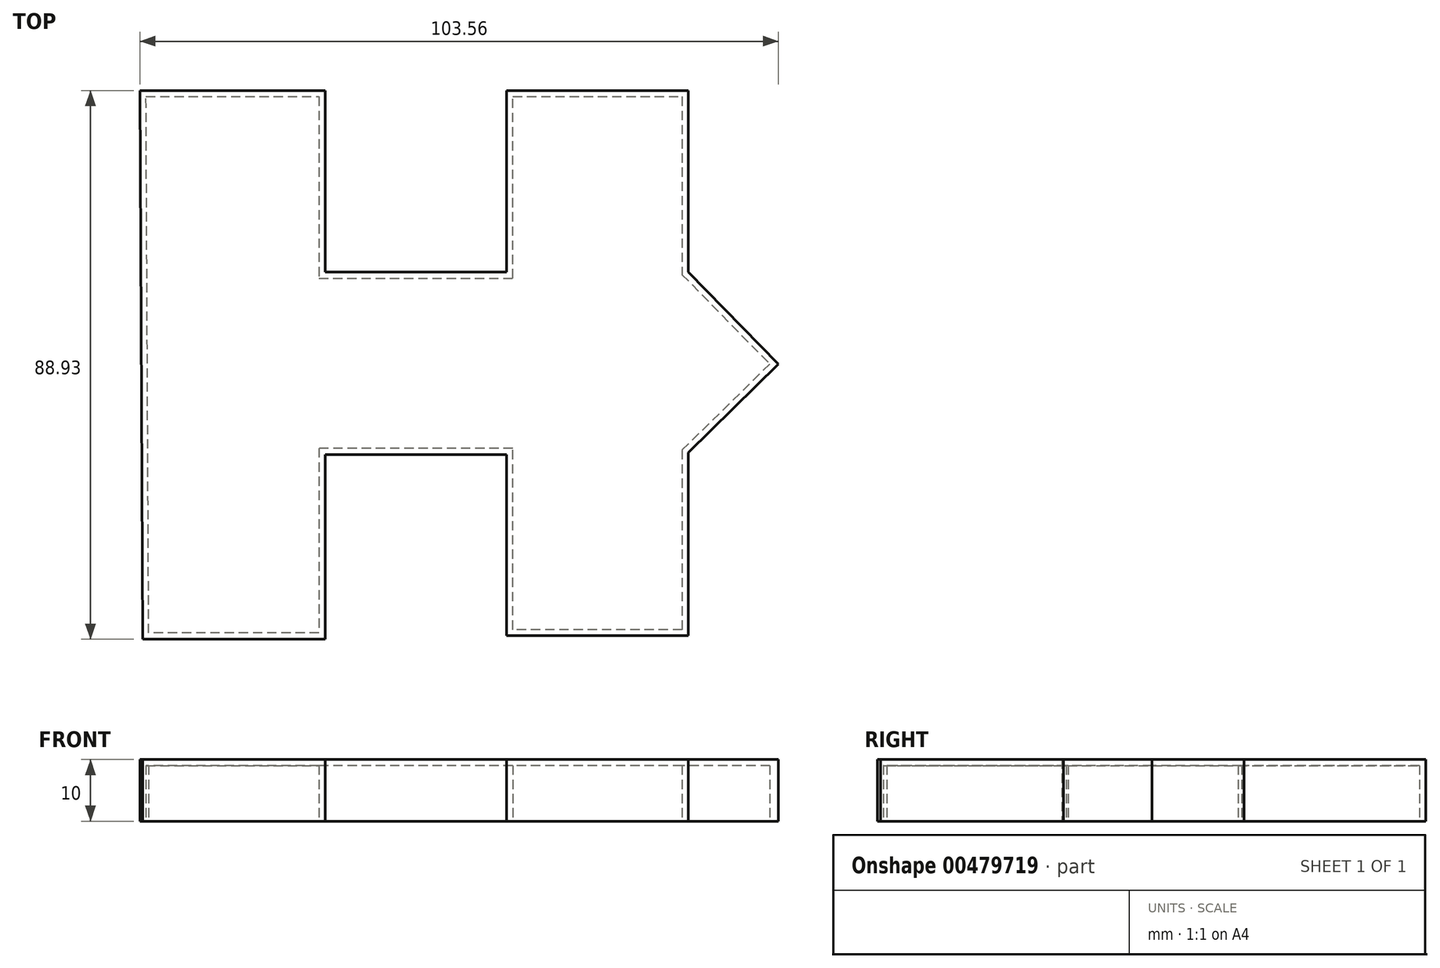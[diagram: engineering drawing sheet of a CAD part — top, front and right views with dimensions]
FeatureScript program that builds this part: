
annotation { "Feature Type Name" : "Feature", "Feature Type Description" : "" }
export const myFeature = defineFeature(function(context is Context, id is Id, definition is map)
    precondition{}
    {
        {
            var Q0;
            Q0=qCreatedBy(makeId("Top.planeOp"),FACE);
            var sketch = newSketch(context, id + "F0", { "sketchPlane" : qUnion([Q0])});
            skLineSegment(sketch, "E0", {"start": v(-44.76, 44.35) * mm, "end": v(-14.71, 44.35) * mm});
            skLineSegment(sketch, "E1", {"start": v(-14.71, 44.35) * mm, "end": v(-14.71, 14.91) * mm});
            skLineSegment(sketch, "E2", {"start": v(-14.71, 14.91) * mm, "end": v(14.73, 14.91) * mm});
            skLineSegment(sketch, "E3", {"start": v(14.73, 14.91) * mm, "end": v(14.73, 44.35) * mm});
            skLineSegment(sketch, "E4", {"start": v(14.73, 44.35) * mm, "end": v(44.17, 44.35) * mm});
            skLineSegment(sketch, "E5", {"start": v(44.17, 44.35) * mm, "end": v(44.17, 14.91) * mm});
            skLineSegment(sketch, "E6", {"start": v(44.17, 14.91) * mm, "end": v(58.8, 0) * mm});
            skLineSegment(sketch, "E7", {"start": v(58.8, 0) * mm, "end": v(44.17, -14.36) * mm});
            skLineSegment(sketch, "E8", {"start": v(44.17, -14.36) * mm, "end": v(44.17, -44.03) * mm});
            skLineSegment(sketch, "E9", {"start": v(44.17, -44.03) * mm, "end": v(14.73, -44.03) * mm});
            skLineSegment(sketch, "E10", {"start": v(14.73, -44.03) * mm, "end": v(14.73, -14.64) * mm});
            skLineSegment(sketch, "E11", {"start": v(14.73, -14.64) * mm, "end": v(-14.71, -14.64) * mm});
            skLineSegment(sketch, "E12", {"start": v(-14.71, -14.64) * mm, "end": v(-14.71, -44.58) * mm});
            skLineSegment(sketch, "E13", {"start": v(-14.71, -44.58) * mm, "end": v(-44.32, -44.58) * mm});
            skLineSegment(sketch, "E14", {"start": v(-44.32, -44.58) * mm, "end": v(-44.76, 44.35) * mm});
            skSolve(sketch);
        }
        {
            var Q0;
            Q0=makeQuery(id+"F0.imprint","IMPRINT",FACE,{"disambiguationData":[TD([[makeQuery(id+"F0.imprint","IMPRINT",EDGE,{"derivedFrom":sQuery(id+"F0.wireOp",EDGE,"E0")}),-1.0]])]});
            extrude(context, id + "F1", {"entities" : qUnion([Q0]), "depth" : 10 * mm});
        }
        {
            var Q0;
            Q0=makeQuery(id+"F1.opExtrude","CAP_FACE",FACE,{"disambiguationData":[OSD([sQuery(id+"F0.wireOp",EDGE,"E0"),sQuery(id+"F0.wireOp",EDGE,"E1"),sQuery(id+"F0.wireOp",EDGE,"E2"),sQuery(id+"F0.wireOp",EDGE,"E3"),sQuery(id+"F0.wireOp",EDGE,"E4"),sQuery(id+"F0.wireOp",EDGE,"E5"),sQuery(id+"F0.wireOp",EDGE,"E6"),sQuery(id+"F0.wireOp",EDGE,"E7"),sQuery(id+"F0.wireOp",EDGE,"E8"),sQuery(id+"F0.wireOp",EDGE,"E9"),sQuery(id+"F0.wireOp",EDGE,"E10"),sQuery(id+"F0.wireOp",EDGE,"E11"),sQuery(id+"F0.wireOp",EDGE,"E12"),sQuery(id+"F0.wireOp",EDGE,"E13"),sQuery(id+"F0.wireOp",EDGE,"E14")])],"isStart":true});
            shell(context, id + "F2", {"entities" : qUnion([Q0]), "thickness" : 1 * mm});
        }
    });
